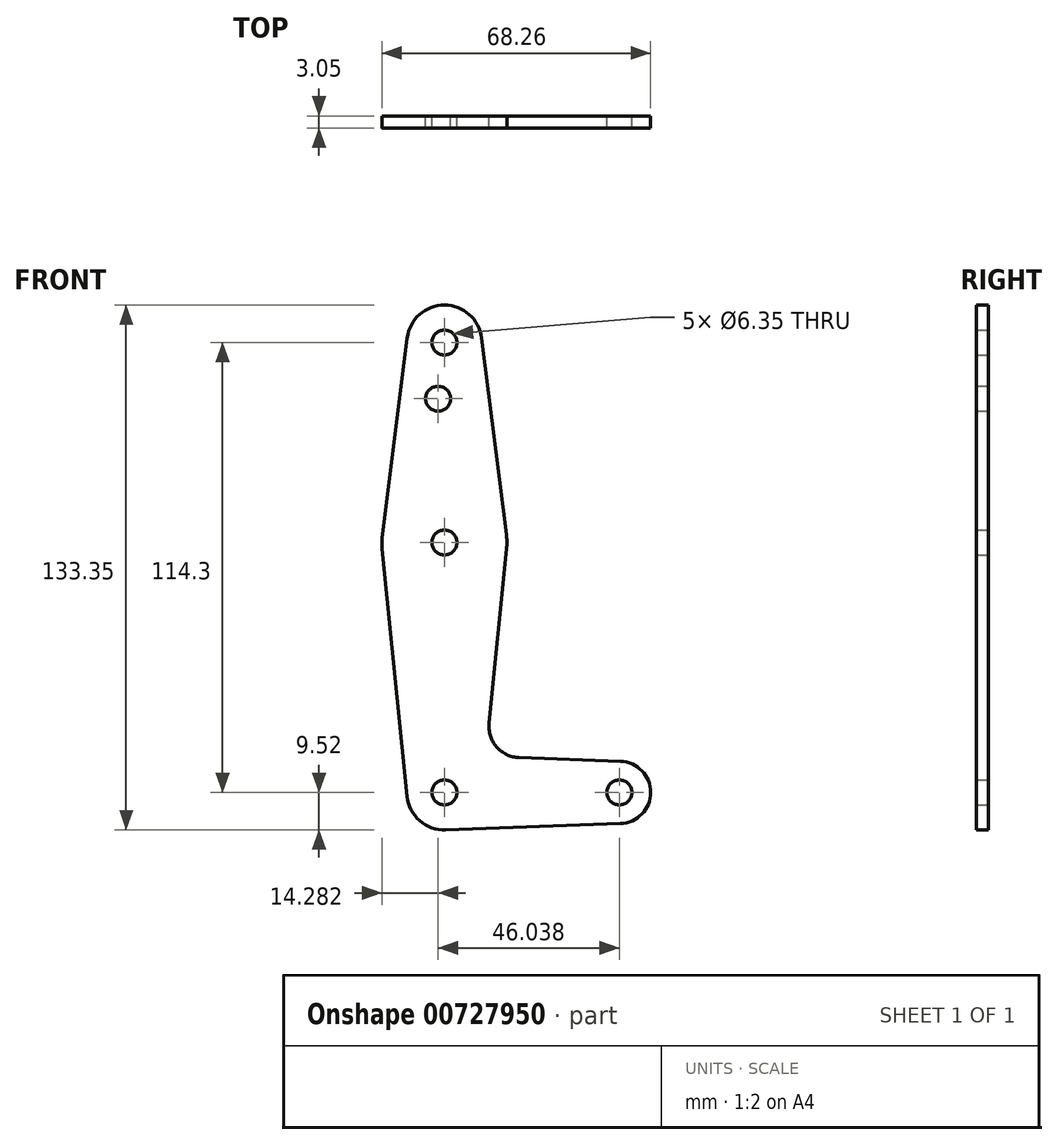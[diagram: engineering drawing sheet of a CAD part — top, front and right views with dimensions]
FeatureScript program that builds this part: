
annotation { "Feature Type Name" : "Feature", "Feature Type Description" : "" }
export const myFeature = defineFeature(function(context is Context, id is Id, definition is map)
    precondition{}
    {
        {
            var Q0;
            Q0=qCreatedBy(makeId("Front.planeOp"),FACE);
            var sketch = newSketch(context, id + "F0", { "sketchPlane" : qUnion([Q0])});
            skLineSegment(sketch, "E0", {"start": v(0, 0) * mm, "end": v(0, 114.3) * mm, "construction": true});
            skLineSegment(sketch, "E1", {"start": v(0, 0) * mm, "end": v(44.45, 0) * mm, "construction": true});
            skCircle(sketch, "E2", {"center": v(0, 114.3) * mm, "radius": 9.53 * mm});
            skCircle(sketch, "E3", {"center": v(0, 63.5) * mm, "radius": 15.88 * mm});
            skCircle(sketch, "E4", {"center": v(0, 0) * mm, "radius": 9.53 * mm});
            skCircle(sketch, "E5", {"center": v(44.45, 0) * mm, "radius": 7.94 * mm});
            skLineSegment(sketch, "E6", {"start": v(9.45, 115.5) * mm, "end": v(15.75, 65.48) * mm});
            skLineSegment(sketch, "E7", {"start": v(15.8, 61.91) * mm, "end": v(11.34, 17.6) * mm});
            skLineSegment(sketch, "E8", {"start": v(-9.45, 115.5) * mm, "end": v(-15.75, 65.48) * mm});
            skLineSegment(sketch, "E9", {"start": v(-15.8, 61.91) * mm, "end": v(-9.48, -0.95) * mm});
            skLineSegment(sketch, "E10", {"start": v(18.97, 8.85) * mm, "end": v(44.73, 7.93) * mm});
            skLineSegment(sketch, "E11", {"start": v(0.34, -9.52) * mm, "end": v(44.73, -7.93) * mm});
            skCircle(sketch, "E12", {"center": v(0, 63.5) * mm, "radius": 3.18 * mm});
            skCircle(sketch, "E13", {"center": v(0, 0) * mm, "radius": 3.18 * mm});
            skCircle(sketch, "E14", {"center": v(44.45, 0) * mm, "radius": 3.18 * mm});
            skCircle(sketch, "E15", {"center": v(0, 114.3) * mm, "radius": 3.18 * mm});
            skCircle(sketch, "E16", {"center": v(-1.59, 100.03) * mm, "radius": 3.18 * mm});
            skArc(sketch, "E17.filletArc", {"start": v(11.34, 17.6) * mm, "mid": v(13.26, 11.57) * mm, "end": v(18.97, 8.85) * mm});
            skSolve(sketch);
        }
        {
            var Q0;
            Q0=makeQuery(id+"F0.imprint","IMPRINT",FACE,{"disambiguationData":[TD([[makeQuery(id+"F0.imprint","IMPRINT",EDGE,{"derivedFrom":sQuery(id+"F0.wireOp",EDGE,"E12")}),-1.0]])]});
            var Q1;
            {var subQ0=sQuery(id+"F0.wireOp",EDGE,"E7");Q1=makeQuery(id+"F0.imprint","IMPRINT",FACE,{"disambiguationData":[TD([[makeQuery(id+"F0.imprint","IMPRINT",EDGE,{"derivedFrom":subQ0}),-1.0]])]});}
            var Q2;
            {var subQ0=sQuery(id+"F0.wireOp",EDGE,"E6");Q2=makeQuery(id+"F0.imprint","IMPRINT",FACE,{"disambiguationData":[TD([[makeQuery(id+"F0.imprint","IMPRINT",EDGE,{"derivedFrom":subQ0}),-1.0]])]});}
            var Q3;
            Q3=makeQuery(id+"F0.imprint","IMPRINT",FACE,{"disambiguationData":[TD([[makeQuery(id+"F0.imprint","IMPRINT",EDGE,{"derivedFrom":sQuery(id+"F0.wireOp",EDGE,"E15")}),-1.0]])]});
            var Q4;
            Q4=makeQuery(id+"F0.imprint","IMPRINT",FACE,{"disambiguationData":[TD([[makeQuery(id+"F0.imprint","IMPRINT",EDGE,{"derivedFrom":sQuery(id+"F0.wireOp",EDGE,"E13")}),-1.0]])]});
            var Q5;
            Q5=makeQuery(id+"F0.imprint","IMPRINT",FACE,{"disambiguationData":[TD([[makeQuery(id+"F0.imprint","IMPRINT",EDGE,{"derivedFrom":sQuery(id+"F0.wireOp",EDGE,"E14")}),-1.0]])]});
            extrude(context, id + "F1", {"entities" : qUnion([Q0, Q1, Q2, Q3, Q4, Q5]), "depth" : 3.05 * mm, "offsetDistance" : 25.4 * mm});
        }
    });
